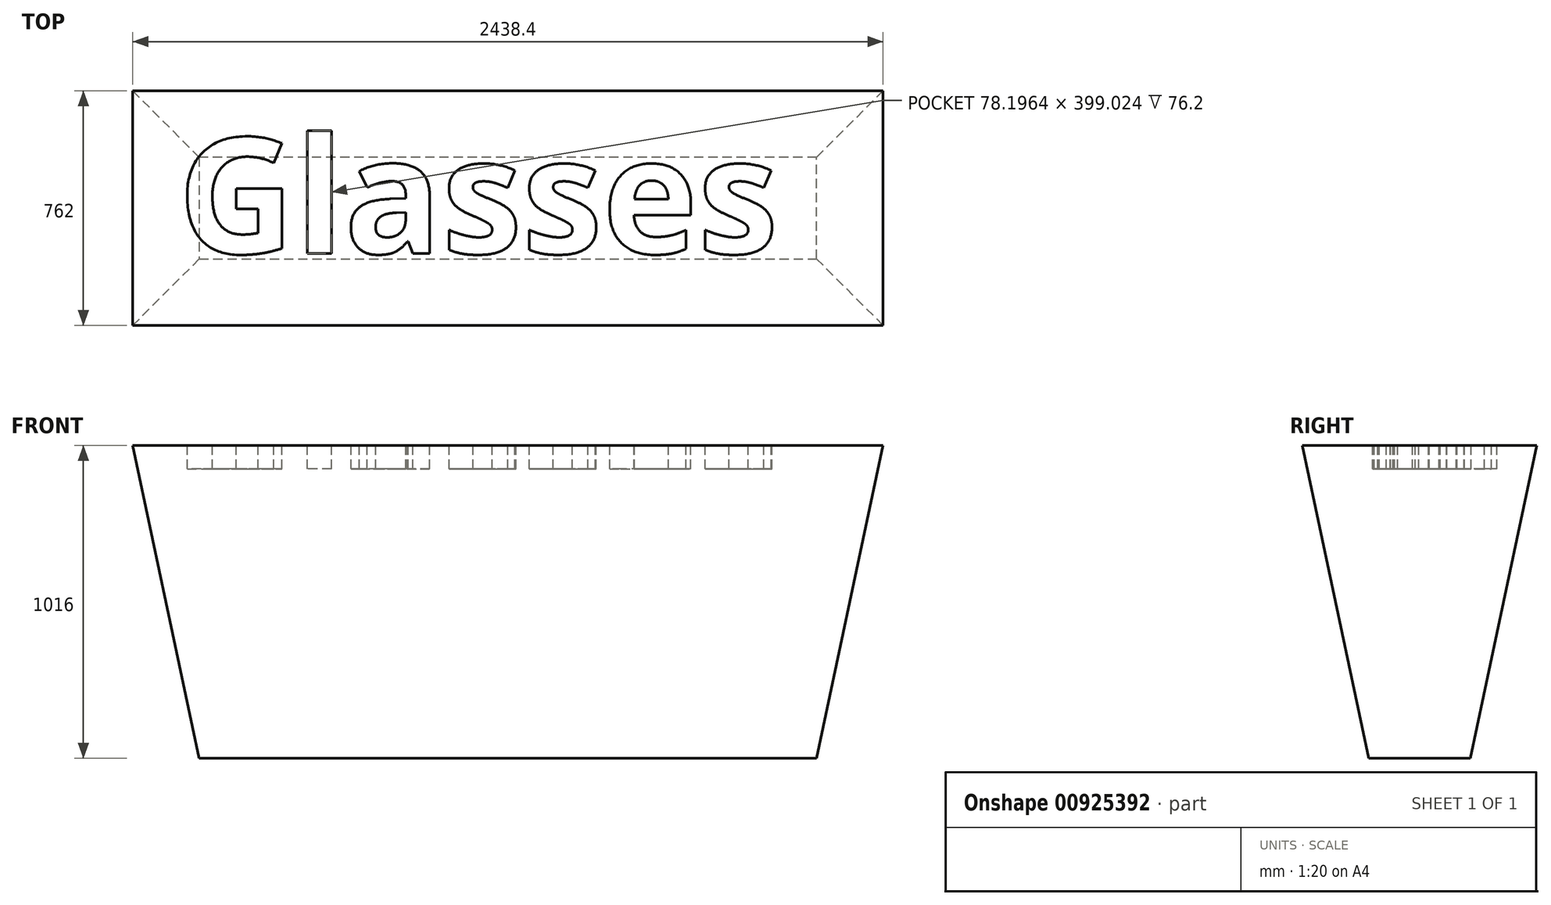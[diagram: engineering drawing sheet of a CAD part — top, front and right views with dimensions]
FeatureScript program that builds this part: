
annotation { "Feature Type Name" : "Feature", "Feature Type Description" : "" }
export const myFeature = defineFeature(function(context is Context, id is Id, definition is map)
    precondition{}
    {
        {
            var Q0;
            Q0=qCreatedBy(makeId("Top.planeOp"),FACE);
            var sketch = newSketch(context, id + "F0", { "sketchPlane" : qUnion([Q0])});
            skLineSegment(sketch, "E0.bottom", {"start": v(1219.2, -381) * mm, "end": v(-1219.2, -381) * mm});
            skLineSegment(sketch, "E0.top", {"start": v(1219.2, 381) * mm, "end": v(-1219.2, 381) * mm});
            skLineSegment(sketch, "E0.left", {"start": v(1219.2, -381) * mm, "end": v(1219.2, 381) * mm});
            skLineSegment(sketch, "E0.right", {"start": v(-1219.2, -381) * mm, "end": v(-1219.2, 381) * mm});
            skPoint(sketch, "E0.middle", {"position": v(0, 0) * mm});
            skSolve(sketch);
        }
        {
            var Q0;
            Q0 = qSketchRegion(id + "F0", true);
            extrude(context, id + "F1", {"entities" : qUnion([Q0]), "oppositeDirection" : true, "depth" : 1016 * mm, "offsetDistance" : 25.4 * mm, "hasDraft" : true, "draftAngle" : 12 * degree, "draftPullDirection" : true});
        }
        {
            var Q0;
            Q0=makeQuery(id+"F1.opExtrude","CAP_FACE",FACE,{"disambiguationData":[OSD([sQuery(id+"F0.wireOp",EDGE,"E0.bottom"),sQuery(id+"F0.wireOp",EDGE,"E0.top"),sQuery(id+"F0.wireOp",EDGE,"E0.left"),sQuery(id+"F0.wireOp",EDGE,"E0.right")])],"isStart":true});
            var sketch = newSketch(context, id + "F2", { "sketchPlane" : qUnion([Q0])});
            skText(sketch, "E1", { "text": "Glasses", "fontName": "OpenSans-Bold.ttf"});
            const initialGuessF2  = {"E1": [-1.07275, -0.14699, 1, 0, 0.3781]};
            skSetInitialGuess(sketch, initialGuessF2);
            skSolve(sketch);
        }
        {
            var Q0;
            Q0 = qSketchRegion(id + "F2", true);
            extrude(context, id + "F3", {"entities" : qUnion([Q0]), "operationType" : NewBodyOperationType.REMOVE, "oppositeDirection" : true, "depth" : 76.2 * mm, "offsetDistance" : 25.4 * mm});
        }
    });
